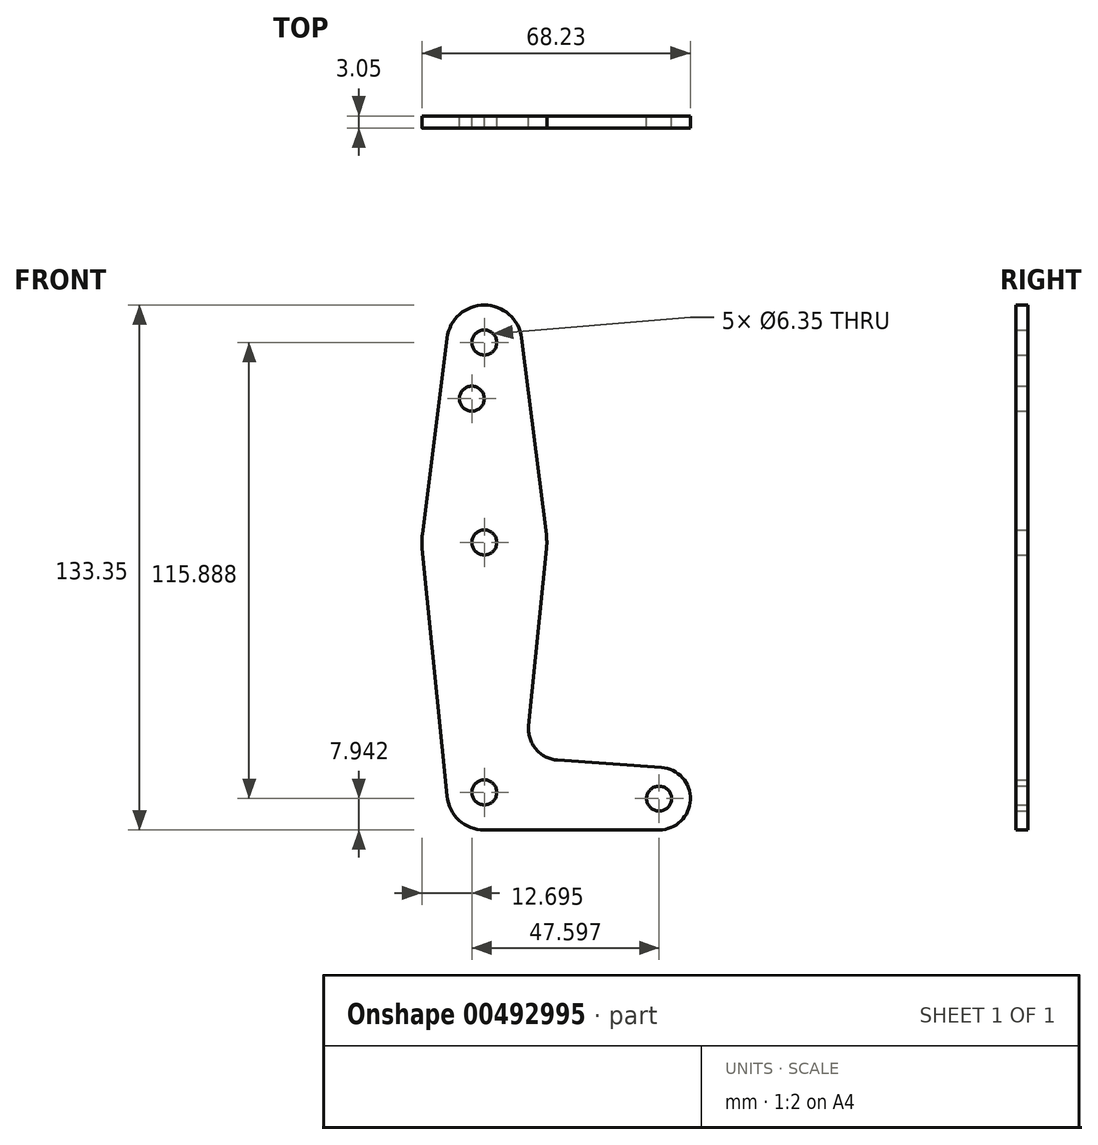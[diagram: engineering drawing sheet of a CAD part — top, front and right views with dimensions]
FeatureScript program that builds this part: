
annotation { "Feature Type Name" : "Feature", "Feature Type Description" : "" }
export const myFeature = defineFeature(function(context is Context, id is Id, definition is map)
    precondition{}
    {
        {
            var Q0;
            Q0=qCreatedBy(makeId("Front.planeOp"),FACE);
            var sketch = newSketch(context, id + "F0", { "sketchPlane" : qUnion([Q0])});
            skCircle(sketch, "E0", {"center": v(0, 50.8) * mm, "radius": 9.53 * mm});
            skCircle(sketch, "E1", {"center": v(0, 0) * mm, "radius": 15.88 * mm});
            skCircle(sketch, "E2", {"center": v(0, -63.5) * mm, "radius": 9.53 * mm});
            skCircle(sketch, "E3", {"center": v(44.42, -65.09) * mm, "radius": 7.94 * mm});
            skLineSegment(sketch, "E4", {"start": v(0, -63.5) * mm, "end": v(44.42, -65.09) * mm});
            skLineSegment(sketch, "E5", {"start": v(0, -63.5) * mm, "end": v(0, 0) * mm, "construction": true});
            skLineSegment(sketch, "E6", {"start": v(0, 0) * mm, "end": v(0, 50.8) * mm, "construction": true});
            skLineSegment(sketch, "E7", {"start": v(9.45, 52) * mm, "end": v(15.75, 1.98) * mm});
            skLineSegment(sketch, "E8", {"start": v(-9.45, 52) * mm, "end": v(-15.75, 1.98) * mm});
            skLineSegment(sketch, "E9", {"start": v(-15.8, -1.59) * mm, "end": v(-9.48, -64.45) * mm});
            skLineSegment(sketch, "E10", {"start": v(18.62, -55.3) * mm, "end": v(44.98, -57.17) * mm});
            skLineSegment(sketch, "E11", {"start": v(0, -73.02) * mm, "end": v(44.42, -73.02) * mm});
            skCircle(sketch, "E12", {"center": v(0, 50.8) * mm, "radius": 3.18 * mm});
            skCircle(sketch, "E13", {"center": v(0, 0) * mm, "radius": 3.18 * mm});
            skCircle(sketch, "E14", {"center": v(0, -63.5) * mm, "radius": 3.18 * mm});
            skCircle(sketch, "E15", {"center": v(44.42, -65.09) * mm, "radius": 3.18 * mm});
            skCircle(sketch, "E16", {"center": v(-3.18, 36.53) * mm, "radius": 3.18 * mm});
            skLineSegment(sketch, "E17", {"start": v(15.8, -1.59) * mm, "end": v(11.27, -46.57) * mm});
            skPoint(sketch, "E18.newPointB", {"position": v(0, -53.98) * mm});
            skArc(sketch, "E18.filletArc", {"start": v(11.27, -46.57) * mm, "mid": v(13.1, -52.49) * mm, "end": v(18.62, -55.3) * mm});
            skSolve(sketch);
        }
        {
            var Q0;
            Q0 = qSketchRegion(id + "F0", true);
            extrude(context, id + "F1", {"entities" : qUnion([Q0]), "depth" : 3.05 * mm});
        }
    });
